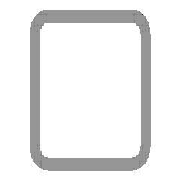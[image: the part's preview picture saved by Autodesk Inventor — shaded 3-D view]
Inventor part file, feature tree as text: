
AUTODESK INVENTOR PART (.ipt)
format: ipt  version: 2021 (Build 250183000, 183)  size: 151,040 bytes
history: native  units: mm (DEFAULTED — no unit token found)
features: other x6, sketch x3, split x2, extrude x1, plane x1
ambient origin geometry x8: Origin, YZ Plane, XZ Plane, XY Plane, X Axis, Y Axis, Z Axis, Center Point
bodies: Solid1 (feature_tree)
feature tree (13):
  parser-record x1  (decoder bookkeeping rows leaked as tree rows — omitted from the tree; the rows remain in map.json)
  other  "Driven Length"
  other  "Plano inicial"
  other  "Plano final"
  extrude  "Corpo"  TaperAngle=0.0deg  [1 undecoded]
  other  "Plano de trabalho4"
  split  "Dividir1"
  other  "Plano de trabalho5"
  split  "Dividir2"
  sketch  "Esboço"  dims[d11=50.8mm d12=4.7625mm d13=-25.4mm d14=4025.4mm d15=25.4mm d16=25.4mm d17=9.525mm d18=90.0deg d19=4050.8mm]
  sketch  "Sketch3"  dims[d3=4050.8mm d4=0.0mm]
  plane  "Work Plane3"
  sketch  "Sketch4"  dims[d10=50.8mm]
note: 1 required parameter value undecoded (feature->parameter linkage not recoverable at this tier; creation-order binding heuristic only, values carry confidence <= 0.55)
